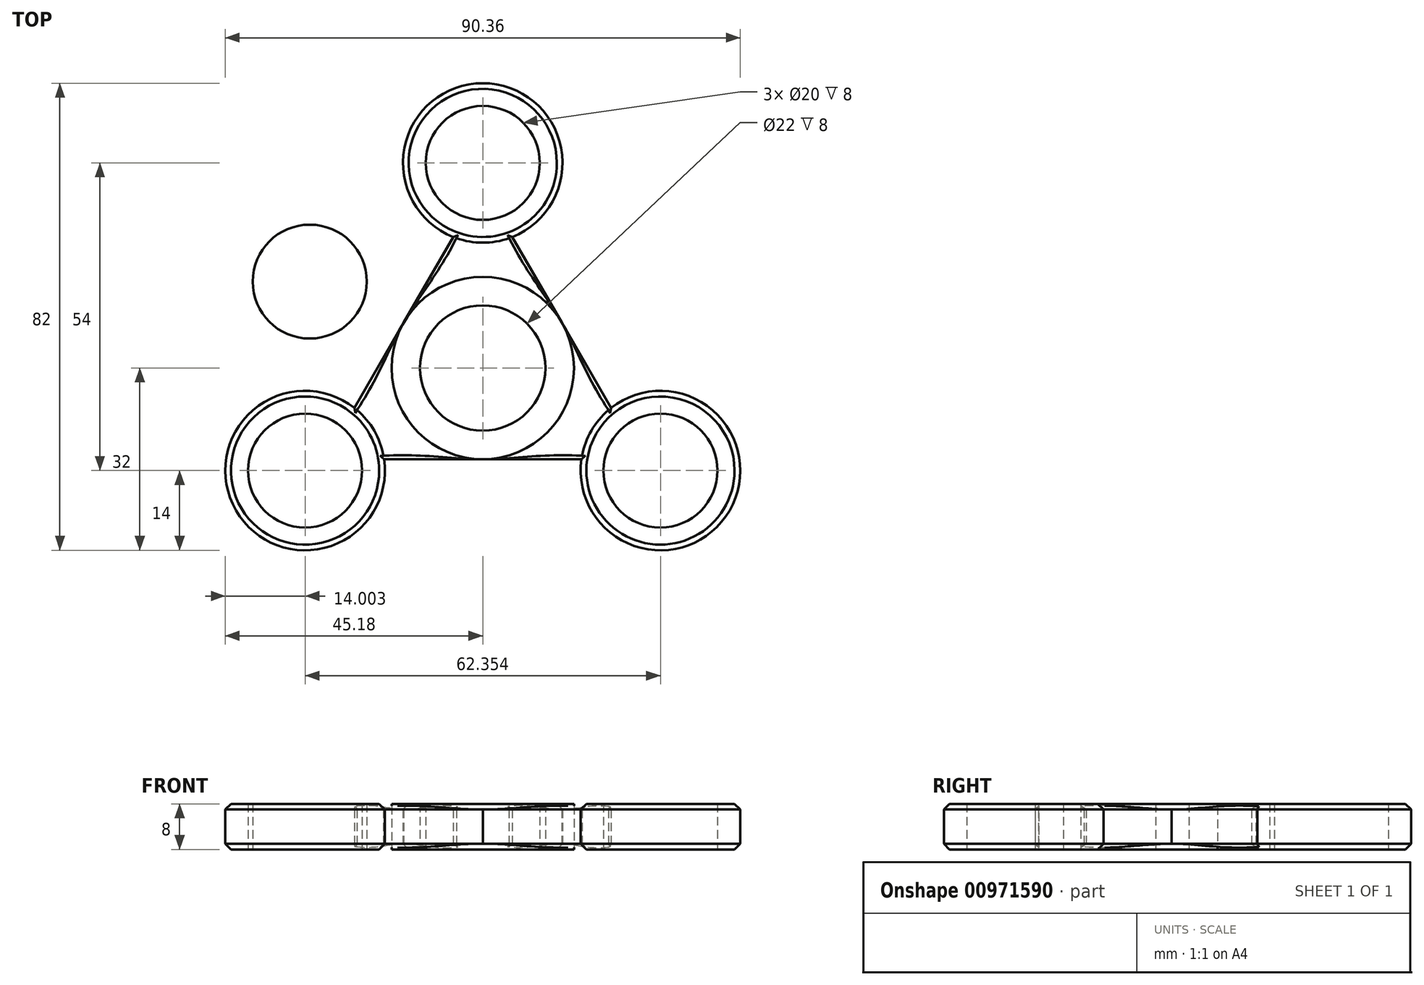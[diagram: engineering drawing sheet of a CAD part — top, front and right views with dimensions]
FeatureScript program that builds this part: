
annotation { "Feature Type Name" : "Feature", "Feature Type Description" : "" }
export const myFeature = defineFeature(function(context is Context, id is Id, definition is map)
    precondition{}
    {
        {
            var Q0;
            Q0=qCreatedBy(makeId("Top.planeOp"),FACE);
            var sketch = newSketch(context, id + "F0", { "sketchPlane" : qUnion([Q0])});
            skCircle(sketch, "E0", {"center": v(0, 0) * mm, "radius": 11 * mm});
            skCircle(sketch, "E1.0.0", {"center": v(0, 0) * mm, "radius": 16 * mm});
            skSolve(sketch);
        }
        {
            var Q0;
            Q0=qCreatedBy(makeId("Top.planeOp"),FACE);
            var sketch = newSketch(context, id + "F1", { "sketchPlane" : qUnion([Q0])});
            skCircle(sketch, "E2", {"center": v(-60.56, 57.57) * mm, "radius": 10 * mm});
            skSolve(sketch);
        }
        {
            var Q0;
            Q0=qCreatedBy(makeId("Top.planeOp"),FACE);
            var sketch = newSketch(context, id + "F2", { "sketchPlane" : qUnion([Q0])});
            skCircle(sketch, "E3.cCircle", {"center": v(0, 0) * mm, "radius": 16 * mm, "construction": true});
            skLineSegment(sketch, "E3.0", {"start": v(0, 32) * mm, "end": v(27.71, -16) * mm});
            skLineSegment(sketch, "E3.1", {"start": v(27.71, -16) * mm, "end": v(-27.71, -16) * mm});
            skLineSegment(sketch, "E3.2", {"start": v(-27.71, -16) * mm, "end": v(0, 32) * mm});
            skPoint(sketch, "E3.0.midPoint", {"position": v(13.86, 8) * mm});
            skCircle(sketch, "E4", {"center": v(0, 0) * mm, "radius": 16 * mm});
            skLineSegment(sketch, "E5", {"start": v(0, 32) * mm, "end": v(0, -16) * mm});
            skLineSegment(sketch, "E6", {"start": v(0, -16) * mm, "end": v(-27.71, -16) * mm});
            skLineSegment(sketch, "E7", {"start": v(-27.71, -16) * mm, "end": v(13.86, 8) * mm});
            skLineSegment(sketch, "E8", {"start": v(27.71, -16) * mm, "end": v(-13.86, 8) * mm});
            skLineSegment(sketch, "E9", {"start": v(-13.86, 8) * mm, "end": v(13.86, 8) * mm});
            skLineSegment(sketch, "E10", {"start": v(0, -16) * mm, "end": v(13.86, 8) * mm});
            skLineSegment(sketch, "E11", {"start": v(-13.86, 8) * mm, "end": v(0, -16) * mm});
            skLineSegment(sketch, "E12", {"start": v(0, 0) * mm, "end": v(0, 26) * mm});
            skLineSegment(sketch, "E13", {"start": v(0, 26) * mm, "end": v(0, 0) * mm});
            skLineSegment(sketch, "E14", {"start": v(0, 0) * mm, "end": v(22.52, -13) * mm});
            skLineSegment(sketch, "E15", {"start": v(19.05, -11) * mm, "end": v(0, 0) * mm});
            skLineSegment(sketch, "E16", {"start": v(0, 0) * mm, "end": v(-22.52, -13) * mm});
            skLineSegment(sketch, "E17", {"start": v(-22.52, -13) * mm, "end": v(0, 0) * mm});
            skCircle(sketch, "E18", {"center": v(-31.18, -18) * mm, "radius": 10 * mm});
            skCircle(sketch, "E19", {"center": v(31.18, -18) * mm, "radius": 10 * mm});
            skCircle(sketch, "E20", {"center": v(0, 36) * mm, "radius": 10 * mm});
            skCircle(sketch, "E21", {"center": v(0, 36) * mm, "radius": 14 * mm});
            skCircle(sketch, "E22", {"center": v(-31.18, -18) * mm, "radius": 14 * mm});
            skCircle(sketch, "E23", {"center": v(31.18, -18) * mm, "radius": 14 * mm});
            skFitSpline(sketch, "E24", {"points": [v(-31.18, -18) * mm, v(-13.86, 8) * mm, v(0, 36) * mm], "startDerivative": vector(66.68, 61.5) * mm, "endDerivative": vector(19.92, 88.5) * mm});
            skFitSpline(sketch, "E25", {"points": [v(0, 36) * mm, v(13.86, 8) * mm, v(31.18, -18) * mm], "startDerivative": vector(19.92, -88.5) * mm, "endDerivative": vector(66.68, -61.5) * mm});
            skFitSpline(sketch, "E26", {"points": [v(-31.18, -18) * mm, v(0, -16) * mm, v(31.18, -18) * mm], "startDerivative": vector(86.6, 27) * mm, "endDerivative": vector(86.6, -27) * mm});
            skSolve(sketch);
        }
        {
            var Q0;
            Q0=makeQuery(id+"F0.imprint","IMPRINT",FACE,{"disambiguationData":[TD([[makeQuery(id+"F0.imprint","IMPRINT",EDGE,{"derivedFrom":sQuery(id+"F0.wireOp",EDGE,"E0")}),-1.0]])]});
            extrude(context, id + "F3", {"entities" : qUnion([Q0]), "depth" : 8 * mm, "offsetDistance" : 25 * mm});
        }
        {
            var Q0;
            Q0 = qSketchRegion(id + "F1", true);
            extrude(context, id + "F4", {"entities" : qUnion([Q0]), "depth" : 8 * mm, "offsetDistance" : 25 * mm});
        }
        {
            var Q0;
            Q0=makeQuery(id+"F2.imprint","IMPRINT",FACE,{"disambiguationData":[TD([[makeQuery(id+"F2.imprint","IMPRINT",EDGE,{"derivedFrom":sQuery(id+"F2.wireOp",EDGE,"E18")}),-1.0]])]});
            var Q1;
            Q1=makeQuery(id+"F2.imprint","IMPRINT",FACE,{"disambiguationData":[TD([[makeQuery(id+"F2.imprint","IMPRINT",EDGE,{"derivedFrom":sQuery(id+"F2.wireOp",EDGE,"E20")}),-1.0]])]});
            var Q2;
            Q2=makeQuery(id+"F2.imprint","IMPRINT",FACE,{"disambiguationData":[TD([[makeQuery(id+"F2.imprint","IMPRINT",EDGE,{"derivedFrom":sQuery(id+"F2.wireOp",EDGE,"E19")}),-1.0]])]});
            var Q3;
            Q3=makeQuery(id+"F2.imprint","IMPRINT",FACE,{"disambiguationData":[TD([[makeQuery(id+"F2.imprint","IMPRINT",EDGE,{"derivedFrom":sQuery(id+"F2.wireOp",EDGE,"870d29b3-9c0a-4a33-a9f1-0f2bd3095fa3.sketch_text.stroke-0")}),1.0]])]});
            var Q4;
            {var subQ1=sQuery(id+"F2.wireOp",EDGE,"E3.2");var subQ3=sQuery(id+"F2.wireOp",EDGE,"E21");var subQ4=makeQuery(id+"F2.imprint","INTERSECT",VERTEX,{"derivedFrom":[subQ1,subQ3]});Q4=makeQuery(id+"F2.imprint","IMPRINT",FACE,{"disambiguationData":[TD([[makeQuery(id+"F2.imprint","IMPRINT",EDGE,{"disambiguationData":[TD([[subQ4,-1.0]])],"derivedFrom":subQ3}),-1.0]])]});}
            var Q5;
            Q5=makeQuery(id+"F2.imprint","IMPRINT",FACE,{"disambiguationData":[TD([[makeQuery(id+"F2.imprint","IMPRINT",EDGE,{"derivedFrom":sQuery(id+"F2.wireOp",EDGE,"870d29b3-9c0a-4a33-a9f1-0f2bd3095fa3.sketch_text.stroke-129")}),1.0]])]});
            var Q6;
            {var subQ1=sQuery(id+"F2.wireOp",EDGE,"E3.0");var subQ3=sQuery(id+"F2.wireOp",EDGE,"E21");var subQ4=makeQuery(id+"F2.imprint","INTERSECT",VERTEX,{"derivedFrom":[subQ1,subQ3]});Q6=makeQuery(id+"F2.imprint","IMPRINT",FACE,{"disambiguationData":[TD([[makeQuery(id+"F2.imprint","IMPRINT",EDGE,{"disambiguationData":[TD([[subQ4,1.0]])],"derivedFrom":subQ3}),-1.0]])]});}
            var Q7;
            {var subQ1=sQuery(id+"F2.wireOp",EDGE,"E3.2");var subQ3=sQuery(id+"F2.wireOp",EDGE,"E22");var subQ4=makeQuery(id+"F2.imprint","INTERSECT",VERTEX,{"derivedFrom":[subQ1,subQ3]});Q7=makeQuery(id+"F2.imprint","IMPRINT",FACE,{"disambiguationData":[TD([[makeQuery(id+"F2.imprint","IMPRINT",EDGE,{"disambiguationData":[TD([[subQ4,1.0]])],"derivedFrom":subQ3}),-1.0]])]});}
            var Q8;
            {var subQ1=sQuery(id+"F2.wireOp",EDGE,"E4");var subQ3=sQuery(id+"F2.wireOp",EDGE,"E17");var subQ4=makeQuery(id+"F2.imprint","INTERSECT",VERTEX,{"derivedFrom":[subQ1,subQ3]});Q8=makeQuery(id+"F2.imprint","IMPRINT",FACE,{"disambiguationData":[TD([[makeQuery(id+"F2.imprint","IMPRINT",EDGE,{"disambiguationData":[TD([[subQ4,1.0]])],"derivedFrom":subQ3}),1.0]])]});}
            var Q9;
            {var subQ1=sQuery(id+"F2.wireOp",EDGE,"E4");var subQ3=sQuery(id+"F2.wireOp",EDGE,"E17");var subQ4=makeQuery(id+"F2.imprint","INTERSECT",VERTEX,{"derivedFrom":[subQ1,subQ3]});Q9=makeQuery(id+"F2.imprint","IMPRINT",FACE,{"disambiguationData":[TD([[makeQuery(id+"F2.imprint","IMPRINT",EDGE,{"disambiguationData":[TD([[subQ4,1.0]])],"derivedFrom":subQ3}),-1.0]])]});}
            var Q10;
            {var subQ1=sQuery(id+"F2.wireOp",EDGE,"E6");var subQ3=sQuery(id+"F2.wireOp",EDGE,"E22");var subQ4=makeQuery(id+"F2.imprint","INTERSECT",VERTEX,{"derivedFrom":[subQ1,subQ3]});Q10=makeQuery(id+"F2.imprint","IMPRINT",FACE,{"disambiguationData":[TD([[makeQuery(id+"F2.imprint","IMPRINT",EDGE,{"disambiguationData":[TD([[subQ4,-1.0]])],"derivedFrom":subQ3}),-1.0]])]});}
            var Q11;
            {var subQ1=sQuery(id+"F2.wireOp",EDGE,"E4");var subQ3=sQuery(id+"F2.wireOp",EDGE,"E15");var subQ4=makeQuery(id+"F2.imprint","INTERSECT",VERTEX,{"derivedFrom":[subQ1,subQ3]});Q11=makeQuery(id+"F2.imprint","IMPRINT",FACE,{"disambiguationData":[TD([[makeQuery(id+"F2.imprint","IMPRINT",EDGE,{"disambiguationData":[TD([[subQ4,1.0]])],"derivedFrom":subQ3}),1.0]])]});}
            var Q12;
            {var subQ1=sQuery(id+"F2.wireOp",EDGE,"E3.1");var subQ3=sQuery(id+"F2.wireOp",EDGE,"E23");var subQ4=makeQuery(id+"F2.imprint","INTERSECT",VERTEX,{"derivedFrom":[subQ1,subQ3]});Q12=makeQuery(id+"F2.imprint","IMPRINT",FACE,{"disambiguationData":[TD([[makeQuery(id+"F2.imprint","IMPRINT",EDGE,{"disambiguationData":[TD([[subQ4,1.0]])],"derivedFrom":subQ3}),-1.0]])]});}
            var Q13;
            {var subQ1=sQuery(id+"F2.wireOp",EDGE,"E4");var subQ3=sQuery(id+"F2.wireOp",EDGE,"E15");var subQ4=makeQuery(id+"F2.imprint","INTERSECT",VERTEX,{"derivedFrom":[subQ1,subQ3]});Q13=makeQuery(id+"F2.imprint","IMPRINT",FACE,{"disambiguationData":[TD([[makeQuery(id+"F2.imprint","IMPRINT",EDGE,{"disambiguationData":[TD([[subQ4,1.0]])],"derivedFrom":subQ3}),-1.0]])]});}
            var Q14;
            {var subQ1=sQuery(id+"F2.wireOp",EDGE,"E3.0");var subQ3=sQuery(id+"F2.wireOp",EDGE,"E23");var subQ4=makeQuery(id+"F2.imprint","INTERSECT",VERTEX,{"derivedFrom":[subQ1,subQ3]});Q14=makeQuery(id+"F2.imprint","IMPRINT",FACE,{"disambiguationData":[TD([[makeQuery(id+"F2.imprint","IMPRINT",EDGE,{"disambiguationData":[TD([[subQ4,-1.0]])],"derivedFrom":subQ3}),-1.0]])]});}
            var Q15;
            {var subQ1=sQuery(id+"F2.wireOp",EDGE,"E4");var subQ3=sQuery(id+"F2.wireOp",EDGE,"E13");var subQ4=makeQuery(id+"F2.imprint","INTERSECT",VERTEX,{"derivedFrom":[subQ1,subQ3]});Q15=makeQuery(id+"F2.imprint","IMPRINT",FACE,{"disambiguationData":[TD([[makeQuery(id+"F2.imprint","IMPRINT",EDGE,{"disambiguationData":[TD([[subQ4,1.0]])],"derivedFrom":subQ3}),-1.0]])]});}
            var Q16;
            {var subQ1=sQuery(id+"F2.wireOp",EDGE,"E4");var subQ3=sQuery(id+"F2.wireOp",EDGE,"E13");var subQ4=makeQuery(id+"F2.imprint","INTERSECT",VERTEX,{"derivedFrom":[subQ1,subQ3]});Q16=makeQuery(id+"F2.imprint","IMPRINT",FACE,{"disambiguationData":[TD([[makeQuery(id+"F2.imprint","IMPRINT",EDGE,{"disambiguationData":[TD([[subQ4,1.0]])],"derivedFrom":subQ3}),1.0]])]});}
            extrude(context, id + "F5", {"entities" : qUnion([Q0, Q1, Q2, Q3, Q4, Q5, Q6, Q7, Q8, Q9, Q10, Q11, Q12, Q13, Q14, Q15, Q16]), "operationType" : NewBodyOperationType.ADD, "depth" : 8 * mm, "offsetDistance" : 25 * mm});
        }
        {
            var Q0;
            Q0=makeQuery(id+"F5.opExtrude","CAP_EDGE",EDGE,{"disambiguationData":[OSD([sQuery(id+"F2.wireOp",EDGE,"E22")])],"isStart":false});
            var Q1;
            Q1=makeQuery(id+"F5.opExtrude","CAP_EDGE",EDGE,{"disambiguationData":[OSD([sQuery(id+"F2.wireOp",EDGE,"E22")])],"isStart":true});
            var Q2;
            Q2=makeQuery(id+"F5.opExtrude","CAP_EDGE",EDGE,{"disambiguationData":[OSD([sQuery(id+"F2.wireOp",EDGE,"E23")])],"isStart":false});
            var Q3;
            Q3=makeQuery(id+"F5.opExtrude","CAP_EDGE",EDGE,{"disambiguationData":[OSD([sQuery(id+"F2.wireOp",EDGE,"E23")])],"isStart":true});
            var Q4;
            Q4=makeQuery(id+"F5.opExtrude","CAP_EDGE",EDGE,{"disambiguationData":[OSD([sQuery(id+"F2.wireOp",EDGE,"E21")])],"isStart":false});
            var Q5;
            Q5=makeQuery(id+"F5.opExtrude","CAP_EDGE",EDGE,{"disambiguationData":[OSD([sQuery(id+"F2.wireOp",EDGE,"E21")])],"isStart":true});
            var Q6;
            Q6=makeQuery(id+"F5.boolean.opBoolean","MERGE",EDGE,{"derivedFrom":[makeQuery(id+"F5.opExtrude","CAP_EDGE",EDGE,{"disambiguationData":[OSD([sQuery(id+"F2.wireOp",EDGE,"E3.1")])],"isStart":false}),makeQuery(id+"F5.opExtrude","CAP_EDGE",EDGE,{"disambiguationData":[OSD([sQuery(id+"F2.wireOp",EDGE,"E6")])],"isStart":false})]});
            var Q7;
            {var subQ0=sQuery(id+"F2.wireOp",EDGE,"E3.2");Q7=makeQuery(id+"F5.boolean.opBoolean","MERGE",EDGE,{"derivedFrom":[makeQuery(id+"F5.opExtrude","CAP_EDGE",EDGE,{"disambiguationData":[OSD([subQ0]),TDD([makeQuery(id+"F2.imprint","IMPRINT",EDGE,{"disambiguationData":[TD([[makeQuery(id+"F2.imprint","INTERSECT",VERTEX,{"derivedFrom":[subQ0,sQuery(id+"F2.wireOp",EDGE,"E22")]}),-1.0]])],"derivedFrom":subQ0})])],"isStart":false}),makeQuery(id+"F5.opExtrude","CAP_EDGE",EDGE,{"disambiguationData":[OSD([subQ0]),TDD([makeQuery(id+"F2.imprint","IMPRINT",EDGE,{"disambiguationData":[TD([[makeQuery(id+"F2.imprint","INTERSECT",VERTEX,{"derivedFrom":[subQ0,sQuery(id+"F2.wireOp",EDGE,"E21")]}),1.0]])],"derivedFrom":subQ0})])],"isStart":false})]});}
            var Q8;
            {var subQ0=sQuery(id+"F2.wireOp",EDGE,"E3.0");Q8=makeQuery(id+"F5.boolean.opBoolean","MERGE",EDGE,{"derivedFrom":[makeQuery(id+"F5.opExtrude","CAP_EDGE",EDGE,{"disambiguationData":[OSD([subQ0]),TDD([makeQuery(id+"F2.imprint","IMPRINT",EDGE,{"disambiguationData":[TD([[makeQuery(id+"F2.imprint","INTERSECT",VERTEX,{"derivedFrom":[subQ0,sQuery(id+"F2.wireOp",EDGE,"E21")]}),-1.0]])],"derivedFrom":subQ0})])],"isStart":false}),makeQuery(id+"F5.opExtrude","CAP_EDGE",EDGE,{"disambiguationData":[OSD([subQ0]),TDD([makeQuery(id+"F2.imprint","IMPRINT",EDGE,{"disambiguationData":[TD([[makeQuery(id+"F2.imprint","INTERSECT",VERTEX,{"derivedFrom":[subQ0,sQuery(id+"F2.wireOp",EDGE,"E23")]}),1.0]])],"derivedFrom":subQ0})])],"isStart":false})]});}
            var Q9;
            {var subQ0=sQuery(id+"F2.wireOp",EDGE,"E3.0");Q9=makeQuery(id+"F5.boolean.opBoolean","MERGE",EDGE,{"derivedFrom":[makeQuery(id+"F5.opExtrude","CAP_EDGE",EDGE,{"disambiguationData":[OSD([subQ0]),TDD([makeQuery(id+"F2.imprint","IMPRINT",EDGE,{"disambiguationData":[TD([[makeQuery(id+"F2.imprint","INTERSECT",VERTEX,{"derivedFrom":[subQ0,sQuery(id+"F2.wireOp",EDGE,"E21")]}),-1.0]])],"derivedFrom":subQ0})])],"isStart":true}),makeQuery(id+"F5.opExtrude","CAP_EDGE",EDGE,{"disambiguationData":[OSD([subQ0]),TDD([makeQuery(id+"F2.imprint","IMPRINT",EDGE,{"disambiguationData":[TD([[makeQuery(id+"F2.imprint","INTERSECT",VERTEX,{"derivedFrom":[subQ0,sQuery(id+"F2.wireOp",EDGE,"E23")]}),1.0]])],"derivedFrom":subQ0})])],"isStart":true})]});}
            var Q10;
            Q10=makeQuery(id+"F5.boolean.opBoolean","MERGE",EDGE,{"derivedFrom":[makeQuery(id+"F5.opExtrude","CAP_EDGE",EDGE,{"disambiguationData":[OSD([sQuery(id+"F2.wireOp",EDGE,"E3.1")])],"isStart":true}),makeQuery(id+"F5.opExtrude","CAP_EDGE",EDGE,{"disambiguationData":[OSD([sQuery(id+"F2.wireOp",EDGE,"E6")])],"isStart":true})]});
            var Q11;
            {var subQ0=sQuery(id+"F2.wireOp",EDGE,"E3.2");Q11=makeQuery(id+"F5.boolean.opBoolean","MERGE",EDGE,{"derivedFrom":[makeQuery(id+"F5.opExtrude","CAP_EDGE",EDGE,{"disambiguationData":[OSD([subQ0]),TDD([makeQuery(id+"F2.imprint","IMPRINT",EDGE,{"disambiguationData":[TD([[makeQuery(id+"F2.imprint","INTERSECT",VERTEX,{"derivedFrom":[subQ0,sQuery(id+"F2.wireOp",EDGE,"E22")]}),-1.0]])],"derivedFrom":subQ0})])],"isStart":true}),makeQuery(id+"F5.opExtrude","CAP_EDGE",EDGE,{"disambiguationData":[OSD([subQ0]),TDD([makeQuery(id+"F2.imprint","IMPRINT",EDGE,{"disambiguationData":[TD([[makeQuery(id+"F2.imprint","INTERSECT",VERTEX,{"derivedFrom":[subQ0,sQuery(id+"F2.wireOp",EDGE,"E21")]}),1.0]])],"derivedFrom":subQ0})])],"isStart":true})]});}
            chamfer(context, id + "F6", {"entities" : qUnion([Q0, Q1, Q2, Q3, Q4, Q5, Q6, Q7, Q8, Q9, Q10, Q11]), "width" : 1 * mm, "tangentPropagation" : true});
        }
        {
            var Q0;
            Q0=makeQuery(id+"F4.opExtrude","SWEPT_BODY",BODY,{"disambiguationData":[OSD([sQuery(id+"F1.wireOp",EDGE,"E2")])]});
            transform(context, id + "F7", {"entities" : qUnion([Q0]), "transformType" : TransformType.TRANSLATION_3D, "dx" : 30.2 * mm, "dy" : -42.4 * mm, "dz" : 0 * mm, "makeCopy" : false});
        }
    });
